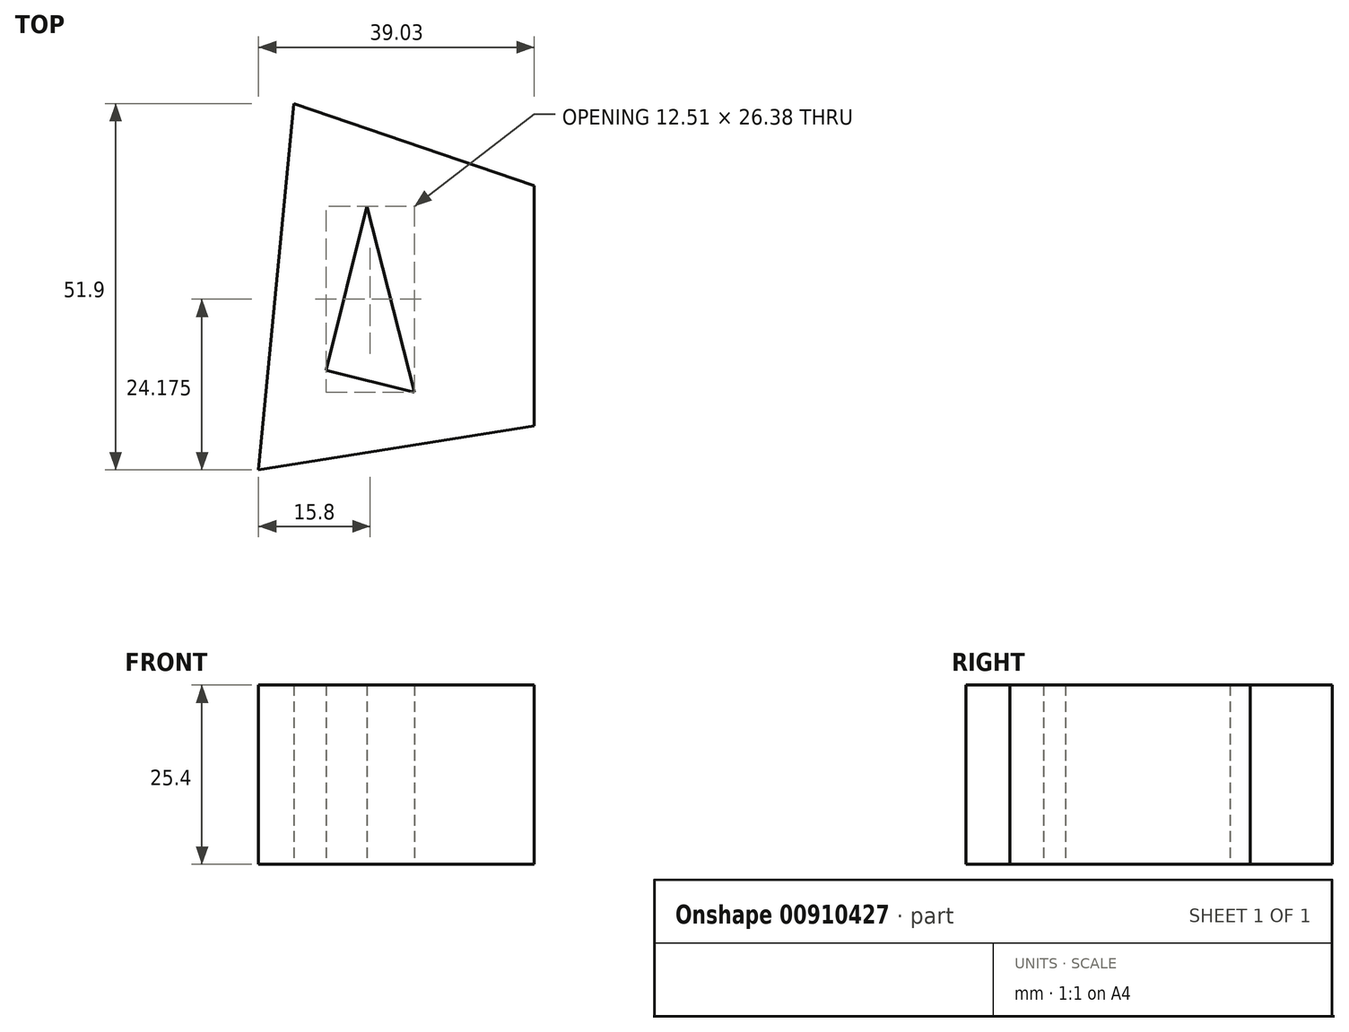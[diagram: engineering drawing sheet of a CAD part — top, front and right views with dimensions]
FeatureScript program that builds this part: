
annotation { "Feature Type Name" : "Feature", "Feature Type Description" : "" }
export const myFeature = defineFeature(function(context is Context, id is Id, definition is map)
    precondition{}
    {
        {
            var Q0;
            Q0=qCreatedBy(makeId("Top.planeOp"),FACE);
            var sketch = newSketch(context, id + "F0", { "sketchPlane" : qUnion([Q0])});
            skCircle(sketch, "E0", {"center": v(-62.28, 52.52) * mm, "radius": 11.18 * mm});
            skLineSegment(sketch, "E1.bottom", {"start": v(23.25, 37.16) * mm, "end": v(59.79, 37.16) * mm});
            skLineSegment(sketch, "E1.top", {"start": v(23.25, 15.57) * mm, "end": v(59.79, 15.57) * mm});
            skLineSegment(sketch, "E1.left", {"start": v(23.25, 37.16) * mm, "end": v(23.25, 15.57) * mm});
            skLineSegment(sketch, "E1.right", {"start": v(59.79, 37.16) * mm, "end": v(59.79, 15.57) * mm});
            skLineSegment(sketch, "E2", {"start": v(-55, -17.45) * mm, "end": v(-20.95, -29.08) * mm});
            skLineSegment(sketch, "E3", {"start": v(-20.95, -29.08) * mm, "end": v(-20.95, -63.13) * mm});
            skLineSegment(sketch, "E4", {"start": v(-20.95, -63.13) * mm, "end": v(-59.98, -69.35) * mm});
            skLineSegment(sketch, "E5", {"start": v(-59.98, -69.35) * mm, "end": v(-55, -17.45) * mm});
            skLineSegment(sketch, "E6", {"start": v(-44.62, -31.99) * mm, "end": v(-50.43, -55.24) * mm});
            skLineSegment(sketch, "E7", {"start": v(-50.43, -55.24) * mm, "end": v(-37.93, -58.36) * mm});
            skLineSegment(sketch, "E8", {"start": v(-37.93, -58.36) * mm, "end": v(-44.62, -31.99) * mm});
            skLineSegment(sketch, "E9", {"start": v(-82.91, 71.7) * mm, "end": v(-82.91, 30.26) * mm, "construction": true});
            skSolve(sketch);
        }
        {
            var Q0;
            Q0=makeQuery(id+"F0.imprint","IMPRINT",FACE,{"disambiguationData":[TD([[makeQuery(id+"F0.imprint","IMPRINT",EDGE,{"derivedFrom":sQuery(id+"F0.wireOp",EDGE,"E2")}),-1.0]])]});
            extrude(context, id + "F1", {"entities" : qUnion([Q0]), "depth" : 25.4 * mm, "offsetDistance" : 25.4 * mm});
        }
    });
